# Revit family: 3079344 Feilo Sylvania Lighting Fixture INST ECO KIT LED BA 36° NW DIMMABLE
name_source: partatom
category: Lighting Fixtures
revit_build: Autodesk Revit 2017 (Build: 20190507_1515(x64)
units: mm (PartAtom-declared; Revit-internal decimal feet)

## family parameters
Cut with Voids When Loaded = No
Host = Face
Light Source = Yes
OmniClass Number = 23.80.70.11.17
OmniClass Title = Specialized Lighting by Location or Use
Part Type = Normal
Room Calculation Point = No
Round Connector Dimension = Use Diameter
Shared = No

## types (1)
- 3079344 INST ECO KIT LED BA 36° NW DIMMABLE
    Apparent Load = 10 VA
    Assembly Code = D5020200
    AssetType = Fixed
    Color Filter = 16777215
    CutoutDiameter_FEILO = 68 mm
    Default Elevation = 0 mm  [stored 0 ft]
    Description = Significant energy savings compared to traditional CFL and 2D fixtures . Excellent flashing provides perfect homogenous light distribution . Unique feature allowing a choice between High Output or High efficiency with the flick of a switch. 50,000 hours life, providing a maintenance free lighting solution . Halo backlight . IP65 fitting resistant to dust and water jet ingress. Tamper resistant locking feature . Ceiling or wall mounted . Integral emergency options suitable for use on defined escape routes. Low profile fitting . Choice of White and Brushed Aluminium trim finishes. Option to add microwave sensor for maximum energy savings
    Diameter_FEILO = 78 mm
    DiffuserDiameter_FEILO = 32 mm
    Dimming Lamp Color Temperature Shift = <None>
    DimmingControlOptions = Dimmable
    DocumentationLiterature = http://www.sylvania-lighting.com
    DurationUnit = hours
    ElectricShockClassification = Class II
    Emit Shape Visible in Rendering = No
    Emit from Circle Diameter = 32 mm
    ExpectedLife = 50000
    HousingRadius_FEILO = 31 mm
    IfcExportAs = IfcLightFixtureType
    IfcExportType = IfcLightFixtureType
    ImpactProtectionIndex = IK02
    IngressProtection = IP44
    InputVoltage = 220-240V~
    Keynote = 16500
    Lamp = LED
    LampColourRenderingIndex = 83
    LampColourTemperature = 4000 K
    LampNominalLuminous = 515 lm
    LampsType = LED
    LightOutputRatio = 100
    LuminousEfficacy = 51.5 lm/W
    Manufacturer = Feilo Sylvania
    ManufacturerName = Feilo Sylvania
    Material = aluminium housing, plastic diffuser
    Material_1_FEILO = Steel_Sylvania_Instar Eco Kit LED Fixed SunDim_Silver
    Material_2_FEILO = Polycarbonate_Sylvania_Instar Eco Kit LED Fixed SunDimi_Clear
    Material_3_FEILO = Steel_Sylvania_Instar Eco Kit LED Fixed SunDim_Silver
    Material_4_FEILO = Steel_Sylvania_Instar Eco Kit LED Fixed SunDim_Silver
    Model = INST ECO KIT LED BA 36° NW DIMMABLE
    ModelNumber = 3079344
    ModelReference = INST ECO KIT LED BA 36° NW DIMMABLE
    Name = INST ECO KIT LED BA 36° NW DIMMABLE
    NominalHeight = 50 mm
    NominalLength = 78 mm
    NominalWidth = 0 mm  [stored 0 ft]
    Photometric Web File = 3079344.ies
    PowerConsumption = 10 W
    PowerFactor = 0
    Radius_FEILO = 39 mm  [stored 0.127953 ft]
    ReflectorDiameter_FEILO = 38 mm
    ReflectorRadius_FEILO = 19 mm
    Tilt Angle = -90°
    TypeName = INST ECO KIT LED BA 36° NW DIMMABLE
    URL = http://www.sylvania-lighting.com
    Voltage = 230 V
    Weight = 7.04 kg

note: [stored X ft] marks values corroborated as IEEE doubles in the binary element streams (Revit-internal decimal feet)

## geometry (parser evidence)
native form markers: Sweep x3
no freeform markers — native parametric forms only
